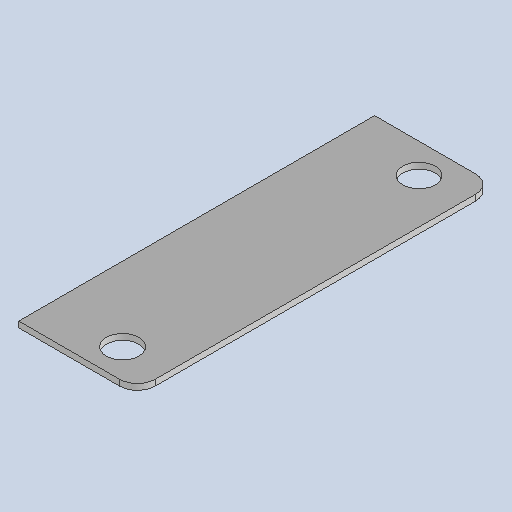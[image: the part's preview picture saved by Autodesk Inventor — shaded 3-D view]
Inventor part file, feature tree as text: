
AUTODESK INVENTOR PART (.ipt)
format: ipt  version: 2025 (Build 290162010, 162A)  size: 222,208 bytes
history: native  units: mm
features: other x4, sketch x2, sheet_metal_op x1, chamfer x1
ambient origin geometry x8: Origin, YZ Plane, XZ Plane, XY Plane, X Axis, Y Axis, Z Axis, Center Point
bodies: Solid1 (feature_tree)
feature tree (8):
  sheet_metal_op  "Face1"
  other  "Mark1"
  other  "A-Side Definition"
  chamfer  "Corner Round1"
  sketch  "Sketch1"  dims[d0=40.0mm]
  other  "Plate1"
  sketch  "Sketch2"  dims[d1=120.0mm d2=2.0mm d6=200.0mm d9=20.0mm d10=20.0mm d11=20.0mm d12=11.0mm d13=100.0mm d14=6.0mm d15=15.0mm]
  other  "Definition1"
